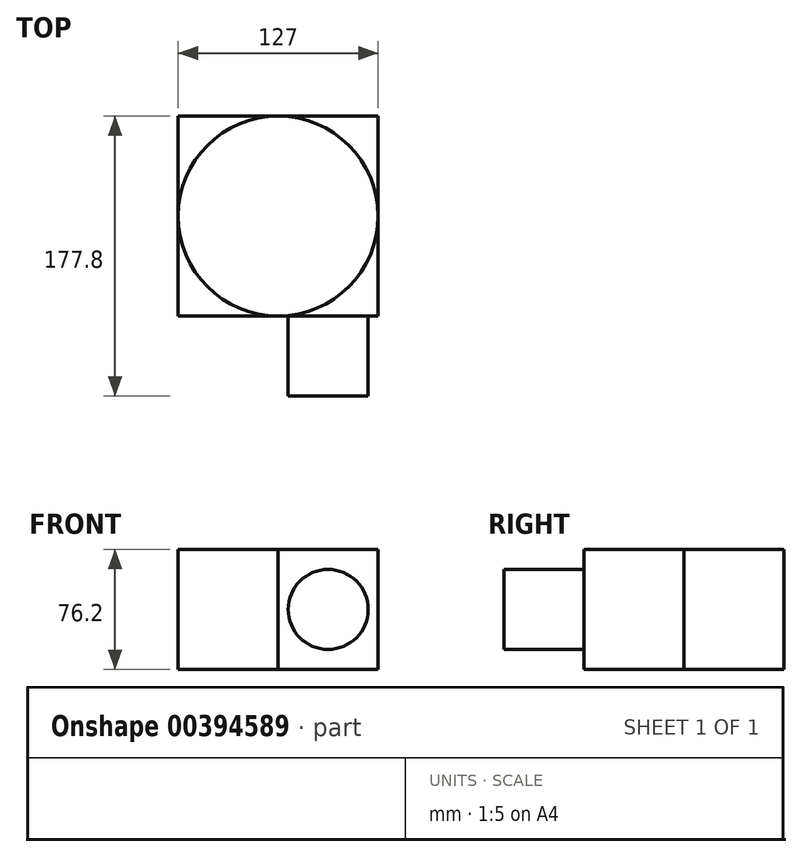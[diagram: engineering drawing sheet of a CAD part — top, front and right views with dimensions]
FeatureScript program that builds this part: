
annotation { "Feature Type Name" : "Feature", "Feature Type Description" : "" }
export const myFeature = defineFeature(function(context is Context, id is Id, definition is map)
    precondition{}
    {
        {
            var Q0;
            Q0=qCreatedBy(makeId("Top.planeOp"),FACE);
            var sketch = newSketch(context, id + "F0", { "sketchPlane" : qUnion([Q0])});
            skLineSegment(sketch, "E0.bottom", {"start": v(0, 0) * mm, "end": v(127, 0) * mm});
            skLineSegment(sketch, "E0.top", {"start": v(0, -127) * mm, "end": v(127, -127) * mm});
            skLineSegment(sketch, "E0.left", {"start": v(0, 0) * mm, "end": v(0, -127) * mm});
            skLineSegment(sketch, "E0.right", {"start": v(127, 0) * mm, "end": v(127, -127) * mm});
            skCircle(sketch, "E1", {"center": v(63.5, -63.5) * mm, "radius": 63.5 * mm});
            skSolve(sketch);
        }
        {
            var Q0;
            {var subQ0=sQuery(id+"F0.wireOp",EDGE,"E0.left");var subQ1=sQuery(id+"F0.wireOp",EDGE,"E0.bottom");var subQ2=makeQuery(id+"F0.imprint","INTERSECT",VERTEX,{"derivedFrom":[subQ1,subQ0]});Q0=makeQuery(id+"F0.imprint","IMPRINT",FACE,{"disambiguationData":[TD([[makeQuery(id+"F0.imprint","IMPRINT",EDGE,{"disambiguationData":[TD([[subQ2,-1.0]])],"derivedFrom":subQ1}),-1.0]])]});}
            var Q1;
            {var subQ0=sQuery(id+"F0.wireOp",EDGE,"E0.right");var subQ1=sQuery(id+"F0.wireOp",EDGE,"E0.bottom");var subQ2=makeQuery(id+"F0.imprint","INTERSECT",VERTEX,{"derivedFrom":[subQ1,subQ0]});Q1=makeQuery(id+"F0.imprint","IMPRINT",FACE,{"disambiguationData":[TD([[makeQuery(id+"F0.imprint","IMPRINT",EDGE,{"disambiguationData":[TD([[subQ2,1.0]])],"derivedFrom":subQ1}),-1.0]])]});}
            var Q2;
            {var subQ0=sQuery(id+"F0.wireOp",EDGE,"E0.left");var subQ1=sQuery(id+"F0.wireOp",EDGE,"E0.top");var subQ2=makeQuery(id+"F0.imprint","INTERSECT",VERTEX,{"derivedFrom":[subQ1,subQ0]});Q2=makeQuery(id+"F0.imprint","IMPRINT",FACE,{"disambiguationData":[TD([[makeQuery(id+"F0.imprint","IMPRINT",EDGE,{"disambiguationData":[TD([[subQ2,-1.0]])],"derivedFrom":subQ1}),1.0]])]});}
            var Q3;
            {var subQ0=sQuery(id+"F0.wireOp",EDGE,"E0.right");var subQ1=sQuery(id+"F0.wireOp",EDGE,"E0.top");var subQ2=makeQuery(id+"F0.imprint","INTERSECT",VERTEX,{"derivedFrom":[subQ1,subQ0]});Q3=makeQuery(id+"F0.imprint","IMPRINT",FACE,{"disambiguationData":[TD([[makeQuery(id+"F0.imprint","IMPRINT",EDGE,{"disambiguationData":[TD([[subQ2,1.0]])],"derivedFrom":subQ1}),1.0]])]});}
            extrude(context, id + "F1", {"entities" : qUnion([Q0, Q1, Q2, Q3]), "depth" : 76.2 * mm});
        }
        {
            var Q0;
            {var subQ0=sQuery(id+"F0.wireOp",EDGE,"E0.top");Q0=makeQuery(id+"F1.opExtrude","SWEPT_FACE",FACE,{"disambiguationData":[OSD([subQ0]),TDD([makeQuery(id+"F0.imprint","IMPRINT",EDGE,{"disambiguationData":[TD([[makeQuery(id+"F0.imprint","INTERSECT",VERTEX,{"derivedFrom":[subQ0,sQuery(id+"F0.wireOp",EDGE,"E0.right")]}),1.0]])],"derivedFrom":subQ0})])]});}
            var sketch = newSketch(context, id + "F2", { "sketchPlane" : qUnion([Q0])});
            skCircle(sketch, "E2", {"center": v(95.25, 38.1) * mm, "radius": 25.4 * mm});
            skSolve(sketch);
        }
        {
            var Q0;
            Q0=makeQuery(id+"F2.imprint","IMPRINT",FACE,{"disambiguationData":[TD([[makeQuery(id+"F2.imprint","IMPRINT",EDGE,{"derivedFrom":sQuery(id+"F2.wireOp",EDGE,"E2")}),1.0]])]});
            extrude(context, id + "F3", {"entities" : qUnion([Q0]), "operationType" : NewBodyOperationType.ADD, "depth" : 50.8 * mm});
        }
    });
